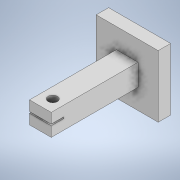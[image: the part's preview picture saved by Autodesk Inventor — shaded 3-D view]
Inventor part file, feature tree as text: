
AUTODESK INVENTOR PART (.ipt)
format: ipt  version: 2021 (Build 250183000, 183)  size: 164,864 bytes
history: native  units: in
note: dims shown in document units (in); Inventor stores cm internally (conversion verified against a paired STEP export)
features: sketch x8, extrude x7
ambient origin geometry x8: Origin, YZ Plane, XZ Plane, XY Plane, X Axis, Y Axis, Z Axis, Center Point
bodies: Solid1 (feature_tree)
feature tree (15):
  extrude  "Extrusion1"  Depth=3.937in
  extrude  "Extrusion2"  Depth=0.0984in
  extrude  "Extrusion3"  Depth=0.6398in
  sketch  "Sketch4"  dims[d7=1.2795in d8=1.2795in]
  extrude  "Extrusion4"  Depth=1.2795in
  extrude  "Extrusion5"  Depth=1.2795in
  extrude  "Extrusion6"  Depth=5.5118in TaperAngle=0.0deg
  extrude  "Extrusion7"  Depth=4.7244in
  sketch  "Sketch1"  dims[d0=3.937in d1=3.937in]
  sketch  "Sketch2"  dims[d2=0.7874in d3=0.0in d4=0.0984in]
  sketch  "Sketch3"  dims[d5=0.6398in d6=0.6398in]
  sketch  "Sketch5"  dims[d9=1.2795in d10=1.2795in]
  sketch  "Sketch6"  dims[d11=1.9193in d12=5.5118in d13=0.0in]
  sketch  "Sketch7"  dims[d14=4.7244in d15=0.5906in]
  sketch  "Sketch8"  dims[d16=0.689in d17=5.9055in d18=0.0in d19=1.378in d20=0.0984in d21=0.0in d22=4.7244in d23=0.0in d24=4.7244in d25=1.0039in d26=0.0984in d27=0.0in d28=0.6398in d29=1.378in d30=5.5118in d31=0.0in d33=0.689in d34=0.5906in d35=4.7244in d36=0.6398in d37=0.0in d32=0.0197in]
